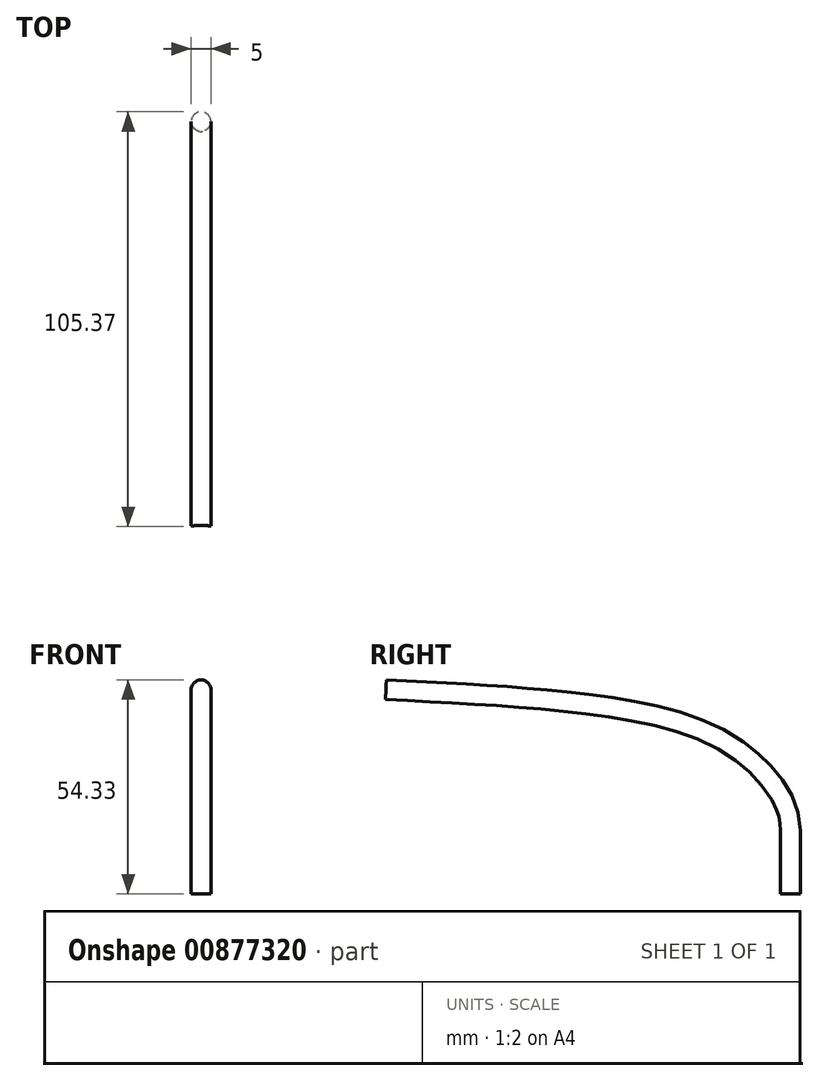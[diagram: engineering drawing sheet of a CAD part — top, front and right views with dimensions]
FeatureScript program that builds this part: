
annotation { "Feature Type Name" : "Feature", "Feature Type Description" : "" }
export const myFeature = defineFeature(function(context is Context, id is Id, definition is map)
    precondition{}
    {
        {
            var Q0;
            Q0=qCreatedBy(makeId("Right.planeOp"),FACE);
            var sketch = newSketch(context, id + "F0", { "sketchPlane" : qUnion([Q0])});
            skFitSpline(sketch, "E0", {"points": [v(0, 16.28) * mm, v(-10.01, 33.9) * mm, v(-33.97, 45.16) * mm, v(-102.9, 51.84) * mm], "startDerivative": vector(0, 79.77) * mm, "endDerivative": vector(-176.8, 8) * mm});
            skLineSegment(sketch, "E1", {"start": v(0, 16.28) * mm, "end": v(0, 0.15) * mm});
            skSolve(sketch);
        }
        {
            var Q0;
            Q0=qCreatedBy(makeId("Top.planeOp"),FACE);
            var sketch = newSketch(context, id + "F1", { "sketchPlane" : qUnion([Q0])});
            skCircle(sketch, "E2", {"center": v(0, 0) * mm, "radius": 2.5 * mm});
            skSolve(sketch);
        }
        {
            var Q0;
            Q0=makeQuery(id+"F1.imprint","IMPRINT",FACE,{"disambiguationData":[TD([[makeQuery(id+"F1.imprint","IMPRINT",EDGE,{"derivedFrom":sQuery(id+"F1.wireOp",EDGE,"E2")}),1.0]])]});
            var Q1;
            Q1=sQuery(id+"F1.wireOp",EDGE,"E2");
            var Q2;
            Q2=sQuery(id+"F0.wireOp",EDGE,"E1");
            var Q3;
            Q3=sQuery(id+"F0.wireOp",EDGE,"E0");
            sweep(context, id + "F2", {"bodyType" : ToolBodyType.SURFACE, "profiles" : qUnion([Q0]), "surfaceProfiles" : qUnion([Q1]), "path" : qUnion([Q2, Q3])});
        }
    });
